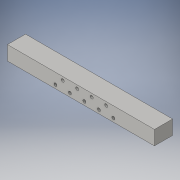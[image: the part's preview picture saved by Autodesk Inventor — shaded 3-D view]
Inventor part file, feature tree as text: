
AUTODESK INVENTOR PART (.ipt)
format: ipt  version: 2016 (Build 200138000, 138)  size: 133,120 bytes
history: native  units: in
note: dims shown in document units (in); Inventor stores cm internally (conversion verified against a paired STEP export)
features: sketch x2, other x1, extrude x1
ambient origin geometry x8: Origin, YZ Plane, XZ Plane, XY Plane, X Axis, Y Axis, Z Axis, Center Point
bodies: Body1 (feature_tree)
feature tree (4):
  other  "Blade.ipt"
  extrude  "Extrusion2"  Depth=0.3937in
  sketch  "Sketch10"  dims[d6=6.0in d7=2.5in d8=0.0in]
  sketch  "Sketch3"  dims[d4=0.3937in d5=4.0in]
